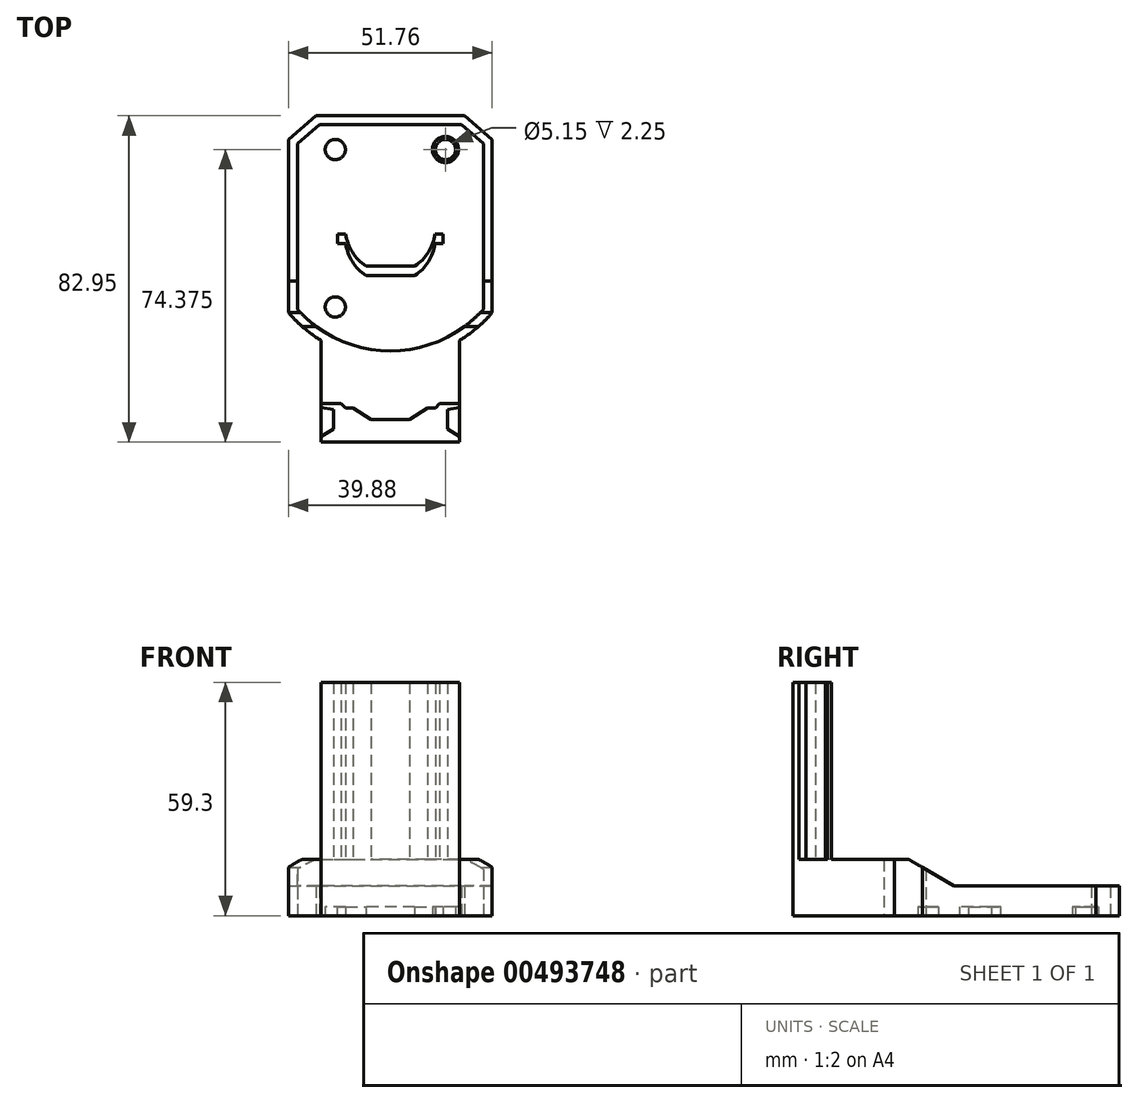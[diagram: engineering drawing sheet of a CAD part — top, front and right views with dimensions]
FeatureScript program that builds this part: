
annotation { "Feature Type Name" : "Feature", "Feature Type Description" : "" }
export const myFeature = defineFeature(function(context is Context, id is Id, definition is map)
    precondition{}
    {
        {
            var Q0;
            Q0=qCreatedBy(makeId("Top.planeOp"),FACE);
            var sketch = newSketch(context, id + "F0", { "sketchPlane" : qUnion([Q0])});
            skLineSegment(sketch, "E0", {"start": v(0, 0) * mm, "end": v(0, 31) * mm});
            skLineSegment(sketch, "E1", {"start": v(0, 31) * mm, "end": v(-18.88, 31) * mm});
            skLineSegment(sketch, "E2", {"start": v(-18.88, 31) * mm, "end": v(-25.88, 25) * mm});
            skLineSegment(sketch, "E3", {"start": v(-25.88, 25) * mm, "end": v(-25.88, -19) * mm});
            skPoint(sketch, "E4", {"position": v(0, -31) * mm});
            skLineSegment(sketch, "E5.MirrorCS", {"start": v(0, 31) * mm, "end": v(18.88, 31) * mm});
            skLineSegment(sketch, "E6.MirrorCS", {"start": v(18.88, 31) * mm, "end": v(25.88, 25) * mm});
            skLineSegment(sketch, "E7.MirrorCS", {"start": v(25.88, 25) * mm, "end": v(25.88, -19) * mm});
            skArc(sketch, "E8", {"start": v(-25.88, -19) * mm, "mid": v(0, -31) * mm, "end": v(25.88, -19) * mm});
            skLineSegment(sketch, "E9", {"start": v(0, 31) * mm, "end": v(0, 28.75) * mm});
            skLineSegment(sketch, "E10", {"start": v(-22.38, 28) * mm, "end": v(-20.91, 26.3) * mm});
            skLineSegment(sketch, "E11", {"start": v(22.38, 28) * mm, "end": v(20.91, 26.3) * mm});
            skLineSegment(sketch, "E12", {"start": v(-25.88, 3) * mm, "end": v(-23.62, 3) * mm});
            skLineSegment(sketch, "E13", {"start": v(25.88, 3) * mm, "end": v(23.62, 3) * mm});
            skLineSegment(sketch, "E14", {"start": v(0, -31) * mm, "end": v(0, -28.75) * mm});
            skLineSegment(sketch, "E15", {"start": v(-25.87, -19) * mm, "end": v(-23.62, -18.16) * mm});
            skLineSegment(sketch, "E16.MirrorCS", {"start": v(25.87, -19) * mm, "end": v(23.62, -18.16) * mm});
            skLineSegment(sketch, "E17", {"start": v(-23.62, -18.16) * mm, "end": v(-23.62, 3) * mm});
            skLineSegment(sketch, "E18", {"start": v(-23.62, 3) * mm, "end": v(-23.62, 23.97) * mm});
            skLineSegment(sketch, "E19", {"start": v(-23.62, 23.97) * mm, "end": v(-20.91, 26.3) * mm});
            skLineSegment(sketch, "E20", {"start": v(-20.91, 26.3) * mm, "end": v(-18.04, 28.75) * mm});
            skLineSegment(sketch, "E21", {"start": v(-18.04, 28.75) * mm, "end": v(0, 28.75) * mm});
            skLineSegment(sketch, "E22", {"start": v(0, 28.75) * mm, "end": v(18.04, 28.75) * mm});
            skLineSegment(sketch, "E23", {"start": v(20.91, 26.3) * mm, "end": v(18.04, 28.75) * mm});
            skLineSegment(sketch, "E24", {"start": v(20.91, 26.3) * mm, "end": v(23.62, 23.97) * mm});
            skLineSegment(sketch, "E25", {"start": v(23.62, 23.97) * mm, "end": v(23.62, 3) * mm});
            skLineSegment(sketch, "E26", {"start": v(23.62, 3) * mm, "end": v(23.62, -18.16) * mm});
            skArc(sketch, "E27", {"start": v(-23.62, -18.16) * mm, "mid": v(0, -28.75) * mm, "end": v(23.62, -18.16) * mm});
            skSolve(sketch);
        }
        {
            var Q0;
            {var subQ1=sQuery(id+"F0.wireOp",EDGE,"E10");Q0=makeQuery(id+"F0.imprint","IMPRINT",FACE,{"disambiguationData":[TD([[makeQuery(id+"F0.imprint","IMPRINT",EDGE,{"derivedFrom":subQ1}),-1.0]])]});}
            var Q1;
            {var subQ2=sQuery(id+"F0.wireOp",EDGE,"E1");Q1=makeQuery(id+"F0.imprint","IMPRINT",FACE,{"disambiguationData":[TD([[makeQuery(id+"F0.imprint","IMPRINT",EDGE,{"derivedFrom":subQ2}),1.0]])]});}
            var Q2;
            {var subQ2=sQuery(id+"F0.wireOp",EDGE,"E5.MirrorCS");Q2=makeQuery(id+"F0.imprint","IMPRINT",FACE,{"disambiguationData":[TD([[makeQuery(id+"F0.imprint","IMPRINT",EDGE,{"derivedFrom":subQ2}),-1.0]])]});}
            var Q3;
            {var subQ1=sQuery(id+"F0.wireOp",EDGE,"E11");Q3=makeQuery(id+"F0.imprint","IMPRINT",FACE,{"disambiguationData":[TD([[makeQuery(id+"F0.imprint","IMPRINT",EDGE,{"derivedFrom":subQ1}),1.0]])]});}
            var Q4;
            {var subQ2=sQuery(id+"F0.wireOp",EDGE,"E13");Q4=makeQuery(id+"F0.imprint","IMPRINT",FACE,{"disambiguationData":[TD([[makeQuery(id+"F0.imprint","IMPRINT",EDGE,{"derivedFrom":subQ2}),1.0]])]});}
            var Q5;
            {var subQ2=sQuery(id+"F0.wireOp",EDGE,"E14");Q5=makeQuery(id+"F0.imprint","IMPRINT",FACE,{"disambiguationData":[TD([[makeQuery(id+"F0.imprint","IMPRINT",EDGE,{"derivedFrom":subQ2}),-1.0]])]});}
            var Q6;
            {var subQ2=sQuery(id+"F0.wireOp",EDGE,"E14");Q6=makeQuery(id+"F0.imprint","IMPRINT",FACE,{"disambiguationData":[TD([[makeQuery(id+"F0.imprint","IMPRINT",EDGE,{"derivedFrom":subQ2}),1.0]])]});}
            var Q7;
            {var subQ2=sQuery(id+"F0.wireOp",EDGE,"E12");Q7=makeQuery(id+"F0.imprint","IMPRINT",FACE,{"disambiguationData":[TD([[makeQuery(id+"F0.imprint","IMPRINT",EDGE,{"derivedFrom":subQ2}),-1.0]])]});}
            extrude(context, id + "F1", {"entities" : qUnion([Q0, Q1, Q2, Q3, Q4, Q5, Q6, Q7]), "depth" : 14.3 * mm});
        }
        {
            var Q0;
            {var subQ1=sQuery(id+"F0.wireOp",EDGE,"E17");Q0=makeQuery(id+"F0.imprint","IMPRINT",FACE,{"disambiguationData":[TD([[makeQuery(id+"F0.imprint","IMPRINT",EDGE,{"derivedFrom":subQ1}),-1.0]])]});}
            extrude(context, id + "F2", {"entities" : qUnion([Q0]), "operationType" : NewBodyOperationType.ADD, "depth" : 2.25 * mm});
        }
        {
            var Q0;
            {var subQ1=sQuery(id+"F0.wireOp",EDGE,"E17");Q0=makeQuery(id+"F0.imprint","IMPRINT",FACE,{"disambiguationData":[TD([[makeQuery(id+"F0.imprint","IMPRINT",EDGE,{"derivedFrom":subQ1}),-1.0]])]});}
            var sketch = newSketch(context, id + "F3", { "sketchPlane" : qUnion([Q0])});
            skCircle(sketch, "E28", {"center": v(14, 22.43) * mm, "radius": 2.58 * mm});
            skCircle(sketch, "E29", {"center": v(14, 22.43) * mm, "radius": 3.3 * mm});
            skCircle(sketch, "E30", {"center": v(14, -17.57) * mm, "radius": 2.58 * mm});
            skCircle(sketch, "E31.MirrorC", {"center": v(-14, 22.43) * mm, "radius": 2.58 * mm});
            skCircle(sketch, "E32.MirrorC", {"center": v(-14, -17.57) * mm, "radius": 2.58 * mm});
            skCircle(sketch, "E33", {"center": v(-14, -17.57) * mm, "radius": 3.3 * mm});
            skLineSegment(sketch, "E34.bottom", {"start": v(-13.37, -1.47) * mm, "end": v(13.37, -1.47) * mm});
            skLineSegment(sketch, "E34.top", {"start": v(-13.37, 1.47) * mm, "end": v(13.37, 1.47) * mm});
            skLineSegment(sketch, "E34.left", {"start": v(-13.37, -1.47) * mm, "end": v(-13.37, 1.47) * mm});
            skLineSegment(sketch, "E34.right", {"start": v(13.37, -1.48) * mm, "end": v(13.37, 1.47) * mm});
            skPoint(sketch, "E34.middle", {"position": v(0, 0) * mm});
            skLineSegment(sketch, "E35.bottom", {"start": v(-6.2, -9.6) * mm, "end": v(6.2, -9.6) * mm});
            skLineSegment(sketch, "E35.top", {"start": v(-6.2, 9.6) * mm, "end": v(6.2, 9.6) * mm});
            skLineSegment(sketch, "E35.left", {"start": v(-6.2, -9.6) * mm, "end": v(-6.2, 9.6) * mm});
            skLineSegment(sketch, "E35.right", {"start": v(6.2, -9.6) * mm, "end": v(6.2, 9.6) * mm});
            skLineSegment(sketch, "E36", {"start": v(13.37, 0) * mm, "end": v(11.42, 0) * mm});
            skPoint(sketch, "E36.endSnap0", {"position": v(13.37, 0) * mm});
            skLineSegment(sketch, "E37", {"start": v(-13.37, 0) * mm, "end": v(-11.42, 0) * mm});
            skPoint(sketch, "E37.endSnap0", {"position": v(-13.37, 0) * mm});
            skArc(sketch, "E38", {"start": v(6.2, -9.6) * mm, "mid": v(11.42, 0) * mm, "end": v(6.2, 9.6) * mm});
            skArc(sketch, "E39", {"start": v(-6.2, 9.6) * mm, "mid": v(-11.42, 0) * mm, "end": v(-6.2, -9.6) * mm});
            skSolve(sketch);
        }
        {
            var Q0;
            Q0=makeQuery(id+"F3.imprint","IMPRINT",FACE,{"disambiguationData":[TD([[makeQuery(id+"F3.imprint","IMPRINT",EDGE,{"derivedFrom":sQuery(id+"F3.wireOp",EDGE,"E32.MirrorC")}),1.0]])]});
            var Q1;
            Q1=makeQuery(id+"F3.imprint","IMPRINT",FACE,{"disambiguationData":[TD([[makeQuery(id+"F3.imprint","IMPRINT",EDGE,{"derivedFrom":sQuery(id+"F3.wireOp",EDGE,"E28")}),-1.0]])]});
            extrude(context, id + "F4", {"entities" : qUnion([Q0, Q1]), "operationType" : NewBodyOperationType.ADD, "depth" : 0.9 * mm});
        }
        {
            var Q0;
            Q0=makeQuery(id+"F3.imprint","IMPRINT",FACE,{"disambiguationData":[TD([[makeQuery(id+"F3.imprint","IMPRINT",EDGE,{"derivedFrom":sQuery(id+"F3.wireOp",EDGE,"E28")}),1.0]])]});
            var Q1;
            Q1=makeQuery(id+"F3.imprint","IMPRINT",FACE,{"disambiguationData":[TD([[makeQuery(id+"F3.imprint","IMPRINT",EDGE,{"derivedFrom":sQuery(id+"F3.wireOp",EDGE,"E31.MirrorC")}),-1.0]])]});
            var Q2;
            Q2=makeQuery(id+"F3.imprint","IMPRINT",FACE,{"disambiguationData":[TD([[makeQuery(id+"F3.imprint","IMPRINT",EDGE,{"derivedFrom":sQuery(id+"F3.wireOp",EDGE,"E32.MirrorC")}),-1.0]])]});
            var Q3;
            Q3=makeQuery(id+"F3.imprint","IMPRINT",FACE,{"disambiguationData":[TD([[makeQuery(id+"F3.imprint","IMPRINT",EDGE,{"derivedFrom":sQuery(id+"F3.wireOp",EDGE,"E30")}),1.0]])]});
            extrude(context, id + "F5", {"entities" : qUnion([Q0, Q1, Q2, Q3]), "operationType" : NewBodyOperationType.REMOVE, "endBound" : BoundingType.THROUGH_ALL, "depth" : 25 * mm});
        }
        {
            var Q0;
            Q0=makeQuery(id+"F2.opExtrude","CAP_FACE",FACE,{"disambiguationData":[OSD([sQuery(id+"F0.wireOp",EDGE,"E17"),sQuery(id+"F0.wireOp",EDGE,"E18"),sQuery(id+"F0.wireOp",EDGE,"E19"),sQuery(id+"F0.wireOp",EDGE,"E20"),sQuery(id+"F0.wireOp",EDGE,"E21"),sQuery(id+"F0.wireOp",EDGE,"E22"),sQuery(id+"F0.wireOp",EDGE,"E23"),sQuery(id+"F0.wireOp",EDGE,"E24"),sQuery(id+"F0.wireOp",EDGE,"E25"),sQuery(id+"F0.wireOp",EDGE,"E26"),sQuery(id+"F0.wireOp",EDGE,"E27")])],"isStart":false});
            var sketch = newSketch(context, id + "F6", { "sketchPlane" : qUnion([Q0])});
            skLineSegment(sketch, "E40.bottom", {"start": v(-13.37, 0.95) * mm, "end": v(13.37, 0.95) * mm});
            skLineSegment(sketch, "E40.top", {"start": v(-13.37, 3.9) * mm, "end": v(13.37, 3.9) * mm});
            skLineSegment(sketch, "E40.left", {"start": v(-13.37, 0.95) * mm, "end": v(-13.37, 3.9) * mm});
            skLineSegment(sketch, "E40.right", {"start": v(13.37, 0.95) * mm, "end": v(13.37, 3.9) * mm});
            skPoint(sketch, "E40.middle", {"position": v(0, 2.42) * mm});
            skLineSegment(sketch, "E41.bottom", {"start": v(-6.2, -7.17) * mm, "end": v(6.2, -7.17) * mm});
            skLineSegment(sketch, "E41.top", {"start": v(-6.2, 12.02) * mm, "end": v(6.2, 12.02) * mm});
            skLineSegment(sketch, "E41.left", {"start": v(-6.2, -7.17) * mm, "end": v(-6.2, 12.02) * mm});
            skLineSegment(sketch, "E41.right", {"start": v(6.2, -7.17) * mm, "end": v(6.2, 12.02) * mm});
            skLineSegment(sketch, "E42", {"start": v(-13.37, 2.43) * mm, "end": v(-11.42, 2.43) * mm});
            skPoint(sketch, "E42.endSnap0", {"position": v(-13.37, 2.43) * mm});
            skArc(sketch, "E43", {"start": v(6.2, -7.17) * mm, "mid": v(11.42, 2.42) * mm, "end": v(6.2, 12.02) * mm});
            skArc(sketch, "E44", {"start": v(-6.2, 12.02) * mm, "mid": v(-11.42, 2.42) * mm, "end": v(-6.2, -7.17) * mm});
            skSolve(sketch);
        }
        {
            var Q0;
            {var subQ5=sQuery(id+"F6.wireOp",EDGE,"E41.top");Q0=makeQuery(id+"F6.imprint","IMPRINT",FACE,{"disambiguationData":[TD([[makeQuery(id+"F6.imprint","IMPRINT",EDGE,{"derivedFrom":subQ5}),-1.0]])]});}
            var Q1;
            {var subQ0=sQuery(id+"F6.wireOp",EDGE,"E44");var subQ1=sQuery(id+"F6.wireOp",EDGE,"E40.top");var subQ2=makeQuery(id+"F6.imprint","INTERSECT",VERTEX,{"derivedFrom":[subQ1,subQ0]});Q1=makeQuery(id+"F6.imprint","IMPRINT",FACE,{"disambiguationData":[TD([[makeQuery(id+"F6.imprint","IMPRINT",EDGE,{"disambiguationData":[TD([[subQ2,-1.0]])],"derivedFrom":subQ1}),1.0]])]});}
            var Q2;
            {var subQ0=sQuery(id+"F6.wireOp",EDGE,"E41.right");var subQ1=sQuery(id+"F6.wireOp",EDGE,"E40.top");var subQ2=makeQuery(id+"F6.imprint","INTERSECT",VERTEX,{"derivedFrom":[subQ1,subQ0]});Q2=makeQuery(id+"F6.imprint","IMPRINT",FACE,{"disambiguationData":[TD([[makeQuery(id+"F6.imprint","IMPRINT",EDGE,{"disambiguationData":[TD([[subQ2,-1.0]])],"derivedFrom":subQ1}),1.0]])]});}
            var Q3;
            {var subQ0=sQuery(id+"F6.wireOp",EDGE,"E41.right");var subQ1=sQuery(id+"F6.wireOp",EDGE,"E40.bottom");var subQ2=makeQuery(id+"F6.imprint","INTERSECT",VERTEX,{"derivedFrom":[subQ1,subQ0]});Q3=makeQuery(id+"F6.imprint","IMPRINT",FACE,{"disambiguationData":[TD([[makeQuery(id+"F6.imprint","IMPRINT",EDGE,{"disambiguationData":[TD([[subQ2,-1.0]])],"derivedFrom":subQ1}),1.0]])]});}
            var Q4;
            {var subQ0=sQuery(id+"F6.wireOp",EDGE,"E40.right");Q4=makeQuery(id+"F6.imprint","IMPRINT",FACE,{"disambiguationData":[TD([[makeQuery(id+"F6.imprint","IMPRINT",EDGE,{"derivedFrom":subQ0}),1.0]])]});}
            var Q5;
            {var subQ0=sQuery(id+"F6.wireOp",EDGE,"E41.right");var subQ1=sQuery(id+"F6.wireOp",EDGE,"E40.bottom");var subQ2=makeQuery(id+"F6.imprint","INTERSECT",VERTEX,{"derivedFrom":[subQ1,subQ0]});Q5=makeQuery(id+"F6.imprint","IMPRINT",FACE,{"disambiguationData":[TD([[makeQuery(id+"F6.imprint","IMPRINT",EDGE,{"disambiguationData":[TD([[subQ2,-1.0]])],"derivedFrom":subQ1}),-1.0]])]});}
            var Q6;
            {var subQ5=sQuery(id+"F6.wireOp",EDGE,"E41.bottom");Q6=makeQuery(id+"F6.imprint","IMPRINT",FACE,{"disambiguationData":[TD([[makeQuery(id+"F6.imprint","IMPRINT",EDGE,{"derivedFrom":subQ5}),1.0]])]});}
            var Q7;
            {var subQ0=sQuery(id+"F6.wireOp",EDGE,"E44");var subQ1=sQuery(id+"F6.wireOp",EDGE,"E40.bottom");var subQ2=makeQuery(id+"F6.imprint","INTERSECT",VERTEX,{"derivedFrom":[subQ1,subQ0]});Q7=makeQuery(id+"F6.imprint","IMPRINT",FACE,{"disambiguationData":[TD([[makeQuery(id+"F6.imprint","IMPRINT",EDGE,{"disambiguationData":[TD([[subQ2,-1.0]])],"derivedFrom":subQ1}),-1.0]])]});}
            var Q8;
            {var subQ0=sQuery(id+"F6.wireOp",EDGE,"E41.left");var subQ1=sQuery(id+"F6.wireOp",EDGE,"E40.bottom");var subQ2=makeQuery(id+"F6.imprint","INTERSECT",VERTEX,{"derivedFrom":[subQ1,subQ0]});Q8=makeQuery(id+"F6.imprint","IMPRINT",FACE,{"disambiguationData":[TD([[makeQuery(id+"F6.imprint","IMPRINT",EDGE,{"disambiguationData":[TD([[subQ2,-1.0]])],"derivedFrom":subQ1}),1.0]])]});}
            var Q9;
            {var subQ0=sQuery(id+"F6.wireOp",EDGE,"E44");var subQ5=sQuery(id+"F6.wireOp",EDGE,"E40.bottom");var subQ8=makeQuery(id+"F6.imprint","INTERSECT",VERTEX,{"derivedFrom":[subQ5,subQ0]});Q9=makeQuery(id+"F6.imprint","IMPRINT",FACE,{"disambiguationData":[TD([[makeQuery(id+"F6.imprint","IMPRINT",EDGE,{"disambiguationData":[TD([[subQ8,-1.0]])],"derivedFrom":subQ5}),1.0]])]});}
            var Q10;
            {var subQ5=sQuery(id+"F6.wireOp",EDGE,"E42");Q10=makeQuery(id+"F6.imprint","IMPRINT",FACE,{"disambiguationData":[TD([[makeQuery(id+"F6.imprint","IMPRINT",EDGE,{"derivedFrom":subQ5}),1.0]])]});}
            var Q11;
            {var subQ5=sQuery(id+"F6.wireOp",EDGE,"E42");Q11=makeQuery(id+"F6.imprint","IMPRINT",FACE,{"disambiguationData":[TD([[makeQuery(id+"F6.imprint","IMPRINT",EDGE,{"derivedFrom":subQ5}),-1.0]])]});}
            extrude(context, id + "F7", {"entities" : qUnion([Q0, Q1, Q2, Q3, Q4, Q5, Q6, Q7, Q8, Q9, Q10, Q11]), "operationType" : NewBodyOperationType.REMOVE, "oppositeDirection" : true, "depth" : 25 * mm});
        }
        {
            var Q0;
            Q0=qCreatedBy(makeId("Front.planeOp"),FACE);
            cPlane(context, id + "F8", {"entities" : qUnion([Q0]), "cplaneType" : CPlaneType.OFFSET, "offset" : 31.85 * mm, "width" : 150 * mm, "height" : 150 * mm});
        }
        {
            var Q0;
            Q0=qCreatedBy(id+"F8.planeOp",FACE);
            var sketch = newSketch(context, id + "F9", { "sketchPlane" : qUnion([Q0])});
            skLineSegment(sketch, "E45.bottom", {"start": v(-17.55, 0) * mm, "end": v(17.55, 0) * mm});
            skLineSegment(sketch, "E45.top", {"start": v(-17.55, 14.3) * mm, "end": v(17.55, 14.3) * mm});
            skLineSegment(sketch, "E45.left", {"start": v(-17.55, 0) * mm, "end": v(-17.55, 14.3) * mm});
            skLineSegment(sketch, "E45.right", {"start": v(17.55, 0) * mm, "end": v(17.55, 14.3) * mm});
            skSolve(sketch);
        }
        {
            var Q0;
            Q0=makeQuery(id+"F9.imprint","IMPRINT",FACE,{"disambiguationData":[TD([[makeQuery(id+"F9.imprint","IMPRINT",EDGE,{"derivedFrom":sQuery(id+"F9.wireOp",EDGE,"E45.bottom")}),1.0]])]});
            extrude(context, id + "F10", {"entities" : qUnion([Q0]), "depth" : 20.1 * mm});
        }
        {
            var Q0;
            Q0=makeQuery(id+"F10.opExtrude","CAP_FACE",FACE,{"disambiguationData":[OSD([sQuery(id+"F9.wireOp",EDGE,"E45.bottom"),sQuery(id+"F9.wireOp",EDGE,"E45.top"),sQuery(id+"F9.wireOp",EDGE,"E45.left"),sQuery(id+"F9.wireOp",EDGE,"E45.right")])],"isStart":true});
            extrude(context, id + "F11", {"entities" : qUnion([Q0]), "operationType" : NewBodyOperationType.ADD, "endBound" : BoundingType.UP_TO_NEXT, "depth" : 25 * mm});
        }
        {
            var Q0;
            Q0=makeQuery(id+"F1.opExtrude","SWEPT_FACE",FACE,{"disambiguationData":[OSD([sQuery(id+"F0.wireOp",EDGE,"E7.MirrorCS")])]});
            var sketch = newSketch(context, id + "F12", { "sketchPlane" : qUnion([Q0])});
            skLineSegment(sketch, "E46", {"start": v(-19, 14.3) * mm, "end": v(-19, 12.3) * mm});
            skLineSegment(sketch, "E47", {"start": v(-19, 12.3) * mm, "end": v(-11, 7.55) * mm});
            skLineSegment(sketch, "E48", {"start": v(-11, 7.55) * mm, "end": v(33.3, 7.55) * mm});
            skLineSegment(sketch, "E49", {"start": v(33.3, 7.55) * mm, "end": v(33.3, 14.3) * mm});
            skLineSegment(sketch, "E50", {"start": v(33.3, 14.3) * mm, "end": v(-22.5, 14.3) * mm});
            skLineSegment(sketch, "E51", {"start": v(-22.5, 14.3) * mm, "end": v(-19, 12.3) * mm});
            skSolve(sketch);
        }
        {
            var Q0;
            {var subQ0=sQuery(id+"F12.wireOp",EDGE,"E46");Q0=makeQuery(id+"F12.imprint","IMPRINT",FACE,{"disambiguationData":[TD([[makeQuery(id+"F12.imprint","IMPRINT",EDGE,{"derivedFrom":subQ0}),-1.0]])]});}
            var Q1;
            {var subQ6=sQuery(id+"F12.wireOp",EDGE,"E46");Q1=makeQuery(id+"F12.imprint","IMPRINT",FACE,{"disambiguationData":[TD([[makeQuery(id+"F12.imprint","IMPRINT",EDGE,{"derivedFrom":subQ6}),1.0]])]});}
            var Q2;
            {var subQ0=sQuery(id+"F12.wireOp",EDGE,"E49");Q2=makeQuery(id+"F12.imprint","IMPRINT",FACE,{"disambiguationData":[TD([[makeQuery(id+"F12.imprint","IMPRINT",EDGE,{"derivedFrom":subQ0}),1.0]])]});}
            extrude(context, id + "F13", {"entities" : qUnion([Q0, Q1, Q2]), "operationType" : NewBodyOperationType.REMOVE, "endBound" : BoundingType.THROUGH_ALL, "oppositeDirection" : true, "depth" : 25 * mm});
        }
        {
            var Q0;
            {var subQ0=sQuery(id+"F9.wireOp",EDGE,"E45.top");Q0=makeQuery(id+"F11.boolean.opBoolean","MERGE",FACE,{"derivedFrom":[makeQuery(id+"F1.opExtrude","CAP_FACE",FACE,{"disambiguationData":[OSD([sQuery(id+"F0.wireOp",EDGE,"E1"),sQuery(id+"F0.wireOp",EDGE,"E2"),sQuery(id+"F0.wireOp",EDGE,"E3"),sQuery(id+"F0.wireOp",EDGE,"E5.MirrorCS"),sQuery(id+"F0.wireOp",EDGE,"E6.MirrorCS"),sQuery(id+"F0.wireOp",EDGE,"E7.MirrorCS"),sQuery(id+"F0.wireOp",EDGE,"E8"),sQuery(id+"F0.wireOp",EDGE,"E17"),sQuery(id+"F0.wireOp",EDGE,"E18"),sQuery(id+"F0.wireOp",EDGE,"E19"),sQuery(id+"F0.wireOp",EDGE,"E20"),sQuery(id+"F0.wireOp",EDGE,"E21"),sQuery(id+"F0.wireOp",EDGE,"E22"),sQuery(id+"F0.wireOp",EDGE,"E23"),sQuery(id+"F0.wireOp",EDGE,"E24"),sQuery(id+"F0.wireOp",EDGE,"E25"),sQuery(id+"F0.wireOp",EDGE,"E26"),sQuery(id+"F0.wireOp",EDGE,"E27")])],"isStart":false}),makeQuery(id+"F10.opExtrude","SWEPT_FACE",FACE,{"disambiguationData":[OSD([subQ0])]}),makeQuery(id+"F11.opExtrude","SWEPT_FACE",FACE,{"disambiguationData":[OSD([subQ0])]})]});}
            var sketch = newSketch(context, id + "F14", { "sketchPlane" : qUnion([Q0])});
            skLineSegment(sketch, "E52", {"start": v(-17.55, -51.95) * mm, "end": v(17.55, -51.95) * mm});
            skLineSegment(sketch, "E53", {"start": v(17.55, -51.95) * mm, "end": v(17.55, -50.45) * mm});
            skLineSegment(sketch, "E54", {"start": v(17.55, -50.45) * mm, "end": v(14.47, -48.65) * mm});
            skLineSegment(sketch, "E55", {"start": v(14.47, -48.65) * mm, "end": v(14.47, -43.6) * mm});
            skLineSegment(sketch, "E56", {"start": v(14.47, -43.6) * mm, "end": v(17.55, -43.15) * mm});
            skLineSegment(sketch, "E57", {"start": v(17.55, -43.15) * mm, "end": v(17.55, -42.15) * mm});
            skLineSegment(sketch, "E58", {"start": v(17.55, -42.15) * mm, "end": v(12.55, -42.15) * mm});
            skLineSegment(sketch, "E59", {"start": v(12.55, -42.15) * mm, "end": v(11.45, -43.25) * mm});
            skLineSegment(sketch, "E60", {"start": v(11.45, -43.25) * mm, "end": v(9.45, -43.25) * mm});
            skLineSegment(sketch, "E61", {"start": v(9.45, -43.25) * mm, "end": v(4.85, -46.2) * mm});
            skLineSegment(sketch, "E62", {"start": v(4.85, -46.2) * mm, "end": v(0, -46.2) * mm});
            skLineSegment(sketch, "E63.MirrorCS", {"start": v(-17.55, -43.15) * mm, "end": v(-17.55, -42.15) * mm});
            skLineSegment(sketch, "E64.MirrorCS", {"start": v(-17.55, -51.95) * mm, "end": v(-17.55, -50.45) * mm});
            skLineSegment(sketch, "E65.MirrorCS", {"start": v(-17.55, -50.45) * mm, "end": v(-14.47, -48.65) * mm});
            skLineSegment(sketch, "E66.MirrorCS", {"start": v(-14.47, -48.65) * mm, "end": v(-14.47, -43.6) * mm});
            skLineSegment(sketch, "E67.MirrorCS", {"start": v(-4.85, -46.2) * mm, "end": v(0, -46.2) * mm});
            skLineSegment(sketch, "E68.MirrorCS", {"start": v(-14.47, -43.6) * mm, "end": v(-17.55, -43.15) * mm});
            skLineSegment(sketch, "E69.MirrorCS", {"start": v(-17.55, -42.15) * mm, "end": v(-12.55, -42.15) * mm});
            skLineSegment(sketch, "E70.MirrorCS", {"start": v(-9.45, -43.25) * mm, "end": v(-4.85, -46.2) * mm});
            skLineSegment(sketch, "E71.MirrorCS", {"start": v(-11.45, -43.25) * mm, "end": v(-9.45, -43.25) * mm});
            skLineSegment(sketch, "E72.MirrorCS", {"start": v(-12.55, -42.15) * mm, "end": v(-11.45, -43.25) * mm});
            skSolve(sketch);
        }
        {
            var Q0;
            Q0=makeQuery(id+"F14.imprint","IMPRINT",FACE,{"disambiguationData":[TD([[makeQuery(id+"F14.imprint","IMPRINT",EDGE,{"derivedFrom":sQuery(id+"F14.wireOp",EDGE,"E52")}),1.0]])]});
            extrude(context, id + "F15", {"entities" : qUnion([Q0]), "operationType" : NewBodyOperationType.ADD, "depth" : 45 * mm});
        }
    });
